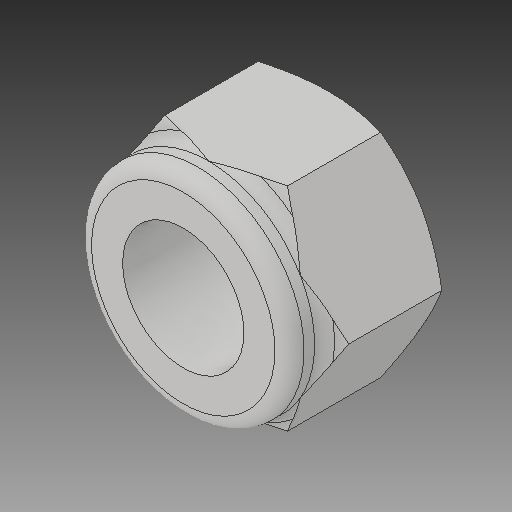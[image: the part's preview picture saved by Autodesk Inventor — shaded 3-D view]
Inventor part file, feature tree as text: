
AUTODESK INVENTOR PART (.ipt)
format: ipt  version: 2017 (Build 210142000, 142)  size: 183,296 bytes
history: native  units: in
note: dims shown in document units (in); Inventor stores cm internally (conversion verified against a paired STEP export)
features: fillet x1
ambient origin geometry x8: Origin, YZ Plane, XZ Plane, XY Plane, X Axis, Y Axis, Z Axis, Center Point
bodies: Solid1 (feature_tree)
feature tree (1):
  fillet  "Fillet7"  [1 undecoded]
note: 1 required parameter value undecoded (feature->parameter linkage not recoverable at this tier; creation-order binding heuristic only, values carry confidence <= 0.55)
